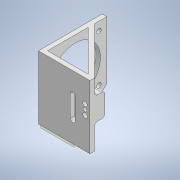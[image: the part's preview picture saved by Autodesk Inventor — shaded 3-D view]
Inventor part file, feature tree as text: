
AUTODESK INVENTOR PART (.ipt)
format: ipt  version: 2022.2 (Build 262287000, 287)  size: 273,408 bytes
history: native  units: mm
features: sketch x8, reference x8, extrude x7, other x6, projected_geometry x5, plane x4, fillet x1
ambient origin geometry x8: Origin, YZ Plane, XZ Plane, XY Plane, X Axis, Y Axis, Z Axis, Center Point
bodies: Solid1 (feature_tree)
feature tree (39):
  extrude  "Extrusion1"  Depth=3.0mm
  sketch  "Sketch5"  dims[d3=3.0mm d4=10.0mm d5=0.0mm]
  plane  "Work Plane1"
  extrude  "Extrusion2"  Depth=10.0mm TaperAngle=0.0deg
  extrude  "Extrusion7"  Depth=10.0mm
  plane  "Work Plane6"
  extrude  "Extrusion3"  Depth=1.59mm
  plane  "Work Plane5"
  extrude  "Extrusion5"  Depth=10.0mm
  plane  "Work Plane3"
  sketch  "Sketch14"  dims[d25=3.0mm d26=45.0deg]
  extrude  "Extrusion9"  TaperAngle=45.0deg  [1 undecoded]
  extrude  "Extrusion10"  TaperAngle=0.0deg  [1 undecoded]
  fillet  "Fillet3"  Radius=2.0mm
  sketch  "Sketch2"  dims[d0=3.0mm d1=0.0mm d2=5.0mm]
  reference  "Reference2"
  reference  "Reference3"
  sketch  "Sketch7"  dims[d11=10.0mm d12=0.0mm d16=4.59mm]
  projected_geometry  "Projected Loop1"
  sketch  "Sketch10"  dims[d17=4.59mm d18=1.59mm]
  reference  "Reference8"
  reference  "Reference9"
  reference  "Reference10"
  reference  "Reference11"
  sketch  "Sketch12"  dims[d19=10.0mm d20=0.0mm d23=2.5mm]
  projected_geometry  "Projected Loop2"
  sketch  "Sketch15"  dims[d27=2.0mm d28=0.0mm d31=0.0mm d32=0.0mm d33=2.0mm d34=0.0mm]
  reference  "Reference12"
  reference  "Reference13"
  projected_geometry  "Projected Loop5"
  sketch  "Sketch16"  dims[d35=2.0mm d24=0.5mm]
  projected_geometry  "Projected Loop6"
  projected_geometry  "Projected Loop7"
  other  "<userpath>\Documents\Inventor\Wire Bender\Assembly.iam"
  other  "Assembly.iam"
  other  "17HM15-0904S:1"
  other  "nema17_top_40mm___ __________4"
  other  "Feed Motor Mount:1"
  other  "Tool Head:1"
note: 2 required parameter values undecoded (feature->parameter linkage not recoverable at this tier; creation-order binding heuristic only, values carry confidence <= 0.55)
